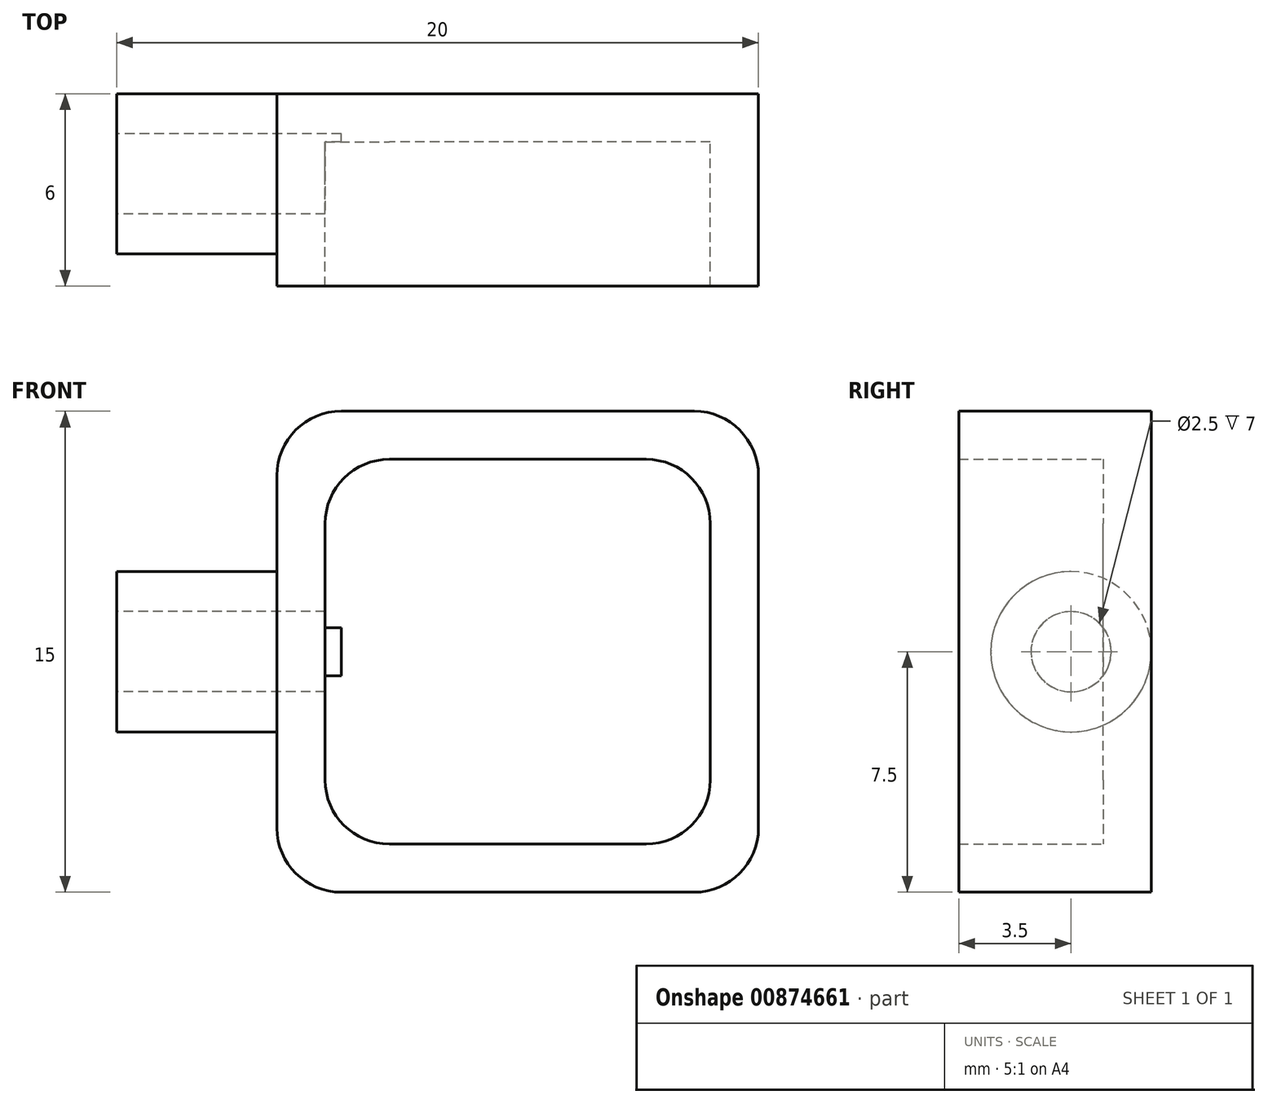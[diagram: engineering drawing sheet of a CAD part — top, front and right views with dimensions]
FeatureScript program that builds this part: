
annotation { "Feature Type Name" : "Feature", "Feature Type Description" : "" }
export const myFeature = defineFeature(function(context is Context, id is Id, definition is map)
    precondition{}
    {
        {
            var Q0;
            Q0=qCreatedBy(makeId("Front.planeOp"),FACE);
            var sketch = newSketch(context, id + "F0", { "sketchPlane" : qUnion([Q0])});
            skLineSegment(sketch, "E0.bottom", {"start": v(4, -6) * mm, "end": v(-4, -6) * mm});
            skLineSegment(sketch, "E0.top", {"start": v(4, 6) * mm, "end": v(-4, 6) * mm});
            skLineSegment(sketch, "E0.left", {"start": v(6, -4) * mm, "end": v(6, 4) * mm});
            skLineSegment(sketch, "E0.right", {"start": v(-6, -4) * mm, "end": v(-6, 4) * mm});
            skPoint(sketch, "E0.middle", {"position": v(0, 0) * mm});
            skLineSegment(sketch, "E1.bottom", {"start": v(5.5, -7.5) * mm, "end": v(-5.5, -7.5) * mm});
            skLineSegment(sketch, "E1.top", {"start": v(5.5, 7.5) * mm, "end": v(-5.5, 7.5) * mm});
            skLineSegment(sketch, "E1.left", {"start": v(7.5, -5.5) * mm, "end": v(7.5, 5.5) * mm});
            skLineSegment(sketch, "E1.right", {"start": v(-7.5, -5.5) * mm, "end": v(-7.5, 5.5) * mm});
            skPoint(sketch, "E2.visualSharp", {"position": v(-7.5, 7.5) * mm});
            skArc(sketch, "E2.filletArc", {"start": v(-5.5, 7.5) * mm, "mid": v(-6.91, 6.91) * mm, "end": v(-7.5, 5.5) * mm});
            skPoint(sketch, "E3.visualSharp", {"position": v(-7.5, -7.5) * mm});
            skArc(sketch, "E3.filletArc", {"start": v(-7.5, -5.5) * mm, "mid": v(-6.91, -6.91) * mm, "end": v(-5.5, -7.5) * mm});
            skPoint(sketch, "E4.visualSharp", {"position": v(7.5, -7.5) * mm});
            skArc(sketch, "E4.filletArc", {"start": v(5.5, -7.5) * mm, "mid": v(6.91, -6.91) * mm, "end": v(7.5, -5.5) * mm});
            skPoint(sketch, "E5.visualSharp", {"position": v(6, -6) * mm});
            skArc(sketch, "E5.filletArc", {"start": v(4, -6) * mm, "mid": v(5.41, -5.41) * mm, "end": v(6, -4) * mm});
            skPoint(sketch, "E6.visualSharp", {"position": v(-6, -6) * mm});
            skArc(sketch, "E6.filletArc", {"start": v(-6, -4) * mm, "mid": v(-5.41, -5.41) * mm, "end": v(-4, -6) * mm});
            skPoint(sketch, "E7.visualSharp", {"position": v(-6, 6) * mm});
            skArc(sketch, "E7.filletArc", {"start": v(-4, 6) * mm, "mid": v(-5.41, 5.41) * mm, "end": v(-6, 4) * mm});
            skPoint(sketch, "E8.visualSharp", {"position": v(6, 6) * mm});
            skArc(sketch, "E8.filletArc", {"start": v(6, 4) * mm, "mid": v(5.41, 5.41) * mm, "end": v(4, 6) * mm});
            skPoint(sketch, "E9.visualSharp", {"position": v(7.5, 7.5) * mm});
            skArc(sketch, "E9.filletArc", {"start": v(7.5, 5.5) * mm, "mid": v(6.91, 6.91) * mm, "end": v(5.5, 7.5) * mm});
            skSolve(sketch);
        }
        {
            var Q0;
            Q0=makeQuery(id+"F0.imprint","IMPRINT",FACE,{"disambiguationData":[TD([[makeQuery(id+"F0.imprint","IMPRINT",EDGE,{"derivedFrom":sQuery(id+"F0.wireOp",EDGE,"E0.bottom")}),-1.0]])]});
            extrude(context, id + "F1", {"entities" : qUnion([Q0]), "depth" : 1.5 * mm, "offsetDistance" : 25 * mm});
        }
        {
            var Q0;
            Q0=makeQuery(id+"F0.imprint","IMPRINT",FACE,{"disambiguationData":[TD([[makeQuery(id+"F0.imprint","IMPRINT",EDGE,{"derivedFrom":sQuery(id+"F0.wireOp",EDGE,"E0.bottom")}),1.0]])]});
            extrude(context, id + "F2", {"entities" : qUnion([Q0]), "operationType" : NewBodyOperationType.ADD, "depth" : 6 * mm, "offsetDistance" : 25 * mm});
        }
        {
            var Q0;
            Q0=makeQuery(id+"F2.opExtrude","SWEPT_FACE",FACE,{"disambiguationData":[OSD([sQuery(id+"F0.wireOp",EDGE,"E1.right")])]});
            var sketch = newSketch(context, id + "F3", { "sketchPlane" : qUnion([Q0])});
            skCircle(sketch, "E10", {"center": v(2.5, 0) * mm, "radius": 1.25 * mm});
            skCircle(sketch, "E11", {"center": v(2.5, 0) * mm, "radius": 2.5 * mm});
            skSolve(sketch);
        }
        {
            var Q0;
            Q0=makeQuery(id+"F3.imprint","IMPRINT",FACE,{"disambiguationData":[TD([[makeQuery(id+"F3.imprint","IMPRINT",EDGE,{"derivedFrom":sQuery(id+"F3.wireOp",EDGE,"E10")}),1.0]])]});
            extrude(context, id + "F4", {"entities" : qUnion([Q0]), "operationType" : NewBodyOperationType.REMOVE, "oppositeDirection" : true, "depth" : 2 * mm, "offsetDistance" : 25 * mm});
        }
        {
            var Q0;
            Q0=makeQuery(id+"F3.imprint","IMPRINT",FACE,{"disambiguationData":[TD([[makeQuery(id+"F3.imprint","IMPRINT",EDGE,{"derivedFrom":sQuery(id+"F3.wireOp",EDGE,"E10")}),-1.0]])]});
            extrude(context, id + "F5", {"entities" : qUnion([Q0]), "operationType" : NewBodyOperationType.ADD, "depth" : 5 * mm, "offsetDistance" : 25 * mm});
        }
    });
